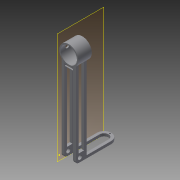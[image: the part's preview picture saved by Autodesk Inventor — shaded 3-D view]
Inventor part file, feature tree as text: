
AUTODESK INVENTOR PART (.ipt)
format: ipt  version: 2015 (Build 190159000, 159)  size: 241,152 bytes
history: native  units: mm
features: sketch x20, extrude x19, plane x3, fillet x1
ambient origin geometry x8: Origin, YZ Plane, XZ Plane, XY Plane, X Axis, Y Axis, Z Axis, Center Point
bodies: Solid1 (feature_tree)
feature tree (43):
  extrude  "Extrusion1"  Depth=2.25mm
  extrude  "Extrusion2"  Depth=2.0mm
  extrude  "Extrusion3"  Depth=2.0mm
  extrude  "Extrusion4"  Depth=2.0mm
  extrude  "Extrusion5"  Depth=2.0mm
  extrude  "Extrusion6"  Depth=2.0mm TaperAngle=0.0deg
  extrude  "Extrusion7"  Depth=2.0mm
  plane  "Work Plane1"
  extrude  "Extrusion8"  Depth=6.0mm
  plane  "Work Plane2"
  extrude  "Extrusion9"  Depth=6.0mm TaperAngle=0.0deg
  extrude  "Extrusion10"  Depth=2.0mm
  extrude  "Extrusion11"  Depth=6.0mm
  extrude  "Extrusion12"  Depth=4.0mm TaperAngle=0.0deg
  extrude  "Extrusion13"  TaperAngle=0.0deg  [1 undecoded]
  extrude  "Extrusion14"  Depth=2.0mm
  extrude  "Extrusion15"  Depth=1.5mm TaperAngle=0.0deg
  extrude  "Extrusion16"  Depth=1.5mm TaperAngle=0.0deg
  fillet  "Fillet4"  Radius=1.0mm
  extrude  "Extrusion17"  Depth=2.0mm
  extrude  "Extrusion18"  Depth=2.0mm
  plane  "Work Plane3"
  sketch  "Sketch19"  dims[d56=59.5mm d57=0.0mm d58=1.0mm d59=0.0mm]
  extrude  "Extrusion19"  Depth=1.0mm TaperAngle=0.0deg
  sketch  "Sketch1"  dims[d0=15.0mm d1=2.25mm]
  sketch  "Sketch2"  dims[d2=2.0mm d3=4.5mm]
  sketch  "Sketch3"  dims[d4=2.0mm d5=10.5mm]
  sketch  "Sketch4"  dims[d6=10.75mm d7=2.0mm]
  sketch  "Sketch5"  dims[d8=13.0mm d9=2.0mm]
  sketch  "Sketch6"  dims[d10=2.0mm d11=60.0mm d12=0.0mm]
  sketch  "Sketch7"  dims[d13=2.0mm d14=6.0mm]
  sketch  "Sketch8"  dims[d15=4.0mm d16=0.0mm d17=6.0mm]
  sketch  "Sketch9"  dims[d18=3.0mm d19=6.0mm d20=0.0mm]
  sketch  "Sketch10"  dims[d22=2.0mm d23=2.0mm]
  sketch  "Sketch11"  dims[d24=20.0mm d25=0.0mm d27=6.0mm]
  sketch  "Sketch12"  dims[d28=4.0mm d29=0.0mm d30=4.0mm d31=0.0mm]
  sketch  "Sketch13"  dims[d33=20.0mm d34=0.0mm d35=0.0mm]
  sketch  "Sketch14"  dims[d36=2.0mm d37=0.0mm d38=60.0mm]
  sketch  "Sketch15"  dims[d42=10.0mm d43=0.0mm d44=1.5mm d45=0.0mm]
  sketch  "Sketch16"  dims[d46=1.0mm d47=0.0mm d48=1.5mm d49=0.0mm d50=1.0mm d51=0.0mm]
  sketch  "Sketch17"  dims[d52=2.0mm d53=2.0mm]
  sketch  "Sketch18"  dims[d54=2.0mm d55=2.0mm]
  sketch  "Sketch20"  dims[d60=1.0mm d61=0.0mm d62=2.0mm d63=1.0mm d64=2.0mm d65=0.0mm d66=1.0mm d67=8.0mm d68=0.0mm d69=0.5mm d70=3.0mm d71=10.0mm d72=0.0mm]
note: 1 required parameter value undecoded (feature->parameter linkage not recoverable at this tier; creation-order binding heuristic only, values carry confidence <= 0.55)
